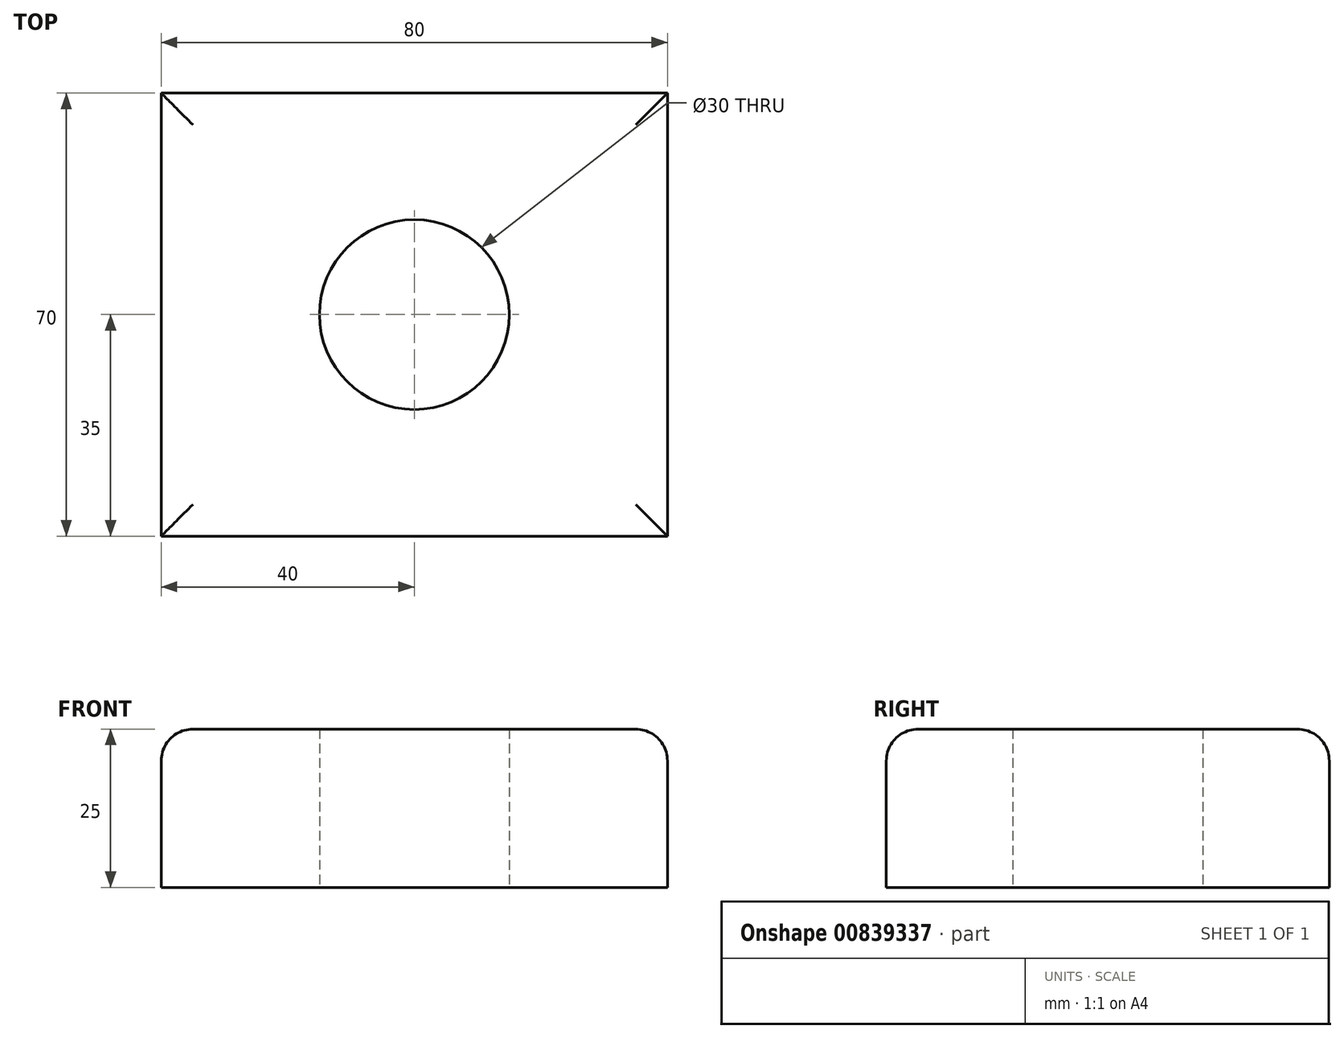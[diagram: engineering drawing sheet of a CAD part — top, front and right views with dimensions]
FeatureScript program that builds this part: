
annotation { "Feature Type Name" : "Feature", "Feature Type Description" : "" }
export const myFeature = defineFeature(function(context is Context, id is Id, definition is map)
    precondition{}
    {
        {
            var Q0;
            Q0=qCreatedBy(makeId("Top.planeOp"),FACE);
            var sketch = newSketch(context, id + "F0", { "sketchPlane" : qUnion([Q0])});
            skCircle(sketch, "E0", {"center": v(0, 0) * mm, "radius": 15 * mm});
            skLineSegment(sketch, "E1.bottom", {"start": v(-40, 35) * mm, "end": v(40, 35) * mm});
            skLineSegment(sketch, "E1.top", {"start": v(-40, -35) * mm, "end": v(40, -35) * mm});
            skLineSegment(sketch, "E1.left", {"start": v(-40, 35) * mm, "end": v(-40, -35) * mm});
            skLineSegment(sketch, "E1.right", {"start": v(40, 35) * mm, "end": v(40, -35) * mm});
            skSolve(sketch);
        }
        {
            var Q0;
            Q0=makeQuery(id+"F0.imprint","IMPRINT",FACE,{"disambiguationData":[TD([[makeQuery(id+"F0.imprint","IMPRINT",EDGE,{"derivedFrom":sQuery(id+"F0.wireOp",EDGE,"E0")}),-1.0]])]});
            extrude(context, id + "F1", {"entities" : qUnion([Q0]), "depth" : 25 * mm, "offsetDistance" : 25 * mm});
        }
        {
            var Q0;
            Q0=makeQuery(id+"F1.opExtrude","CAP_EDGE",EDGE,{"disambiguationData":[OSD([sQuery(id+"F0.wireOp",EDGE,"E1.left")])],"isStart":false});
            var Q1;
            Q1=makeQuery(id+"F1.opExtrude","CAP_EDGE",EDGE,{"disambiguationData":[OSD([sQuery(id+"F0.wireOp",EDGE,"E1.top")])],"isStart":false});
            var Q2;
            Q2=makeQuery(id+"F1.opExtrude","CAP_EDGE",EDGE,{"disambiguationData":[OSD([sQuery(id+"F0.wireOp",EDGE,"E1.right")])],"isStart":false});
            var Q3;
            Q3=makeQuery(id+"F1.opExtrude","CAP_EDGE",EDGE,{"disambiguationData":[OSD([sQuery(id+"F0.wireOp",EDGE,"E1.bottom")])],"isStart":false});
            fillet(context, id + "F2", {"entities" : qUnion([Q0, Q1, Q2, Q3]), "radius" : 5 * mm, "tangentPropagation" : true, "allowEdgeOverflow" : false});
        }
        {
            var Q0;
            Q0=qCreatedBy(makeId("Top.planeOp"),FACE);
            cPlane(context, id + "F3", {"entities" : qUnion([Q0]), "cplaneType" : CPlaneType.OFFSET, "offset" : 25 * mm, "width" : 150 * mm, "height" : 150 * mm});
        }
    });
